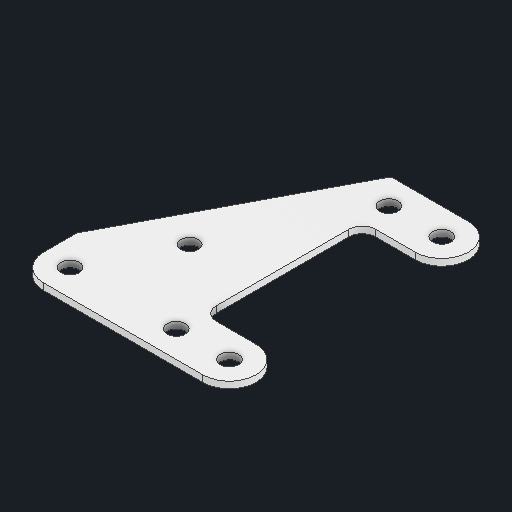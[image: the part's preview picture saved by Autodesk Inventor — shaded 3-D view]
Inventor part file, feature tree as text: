
AUTODESK INVENTOR PART (.ipt)
format: ipt  version: 2025 (Build 290162000, 162)  size: 126,976 bytes
history: native  units: in
note: dims shown in document units (in); Inventor stores cm internally (conversion verified against a paired STEP export)
features: other x3, extrude x1, sketch x1
ambient origin geometry x8: Origin, YZ Plane, XZ Plane, XY Plane, X Axis, Y Axis, Z Axis, Center Point
bodies: Solid1 (feature_tree)
feature tree (5):
  other  "Blocks"
  extrude  "Extrusion1"  Depth=0.0625in TaperAngle=0.0deg
  sketch  "Sketch1"  dims[d0=0.125in d1=0.0625in d2=0.0in d3=0.165in]
  other  "main"
  other  "main:1"
